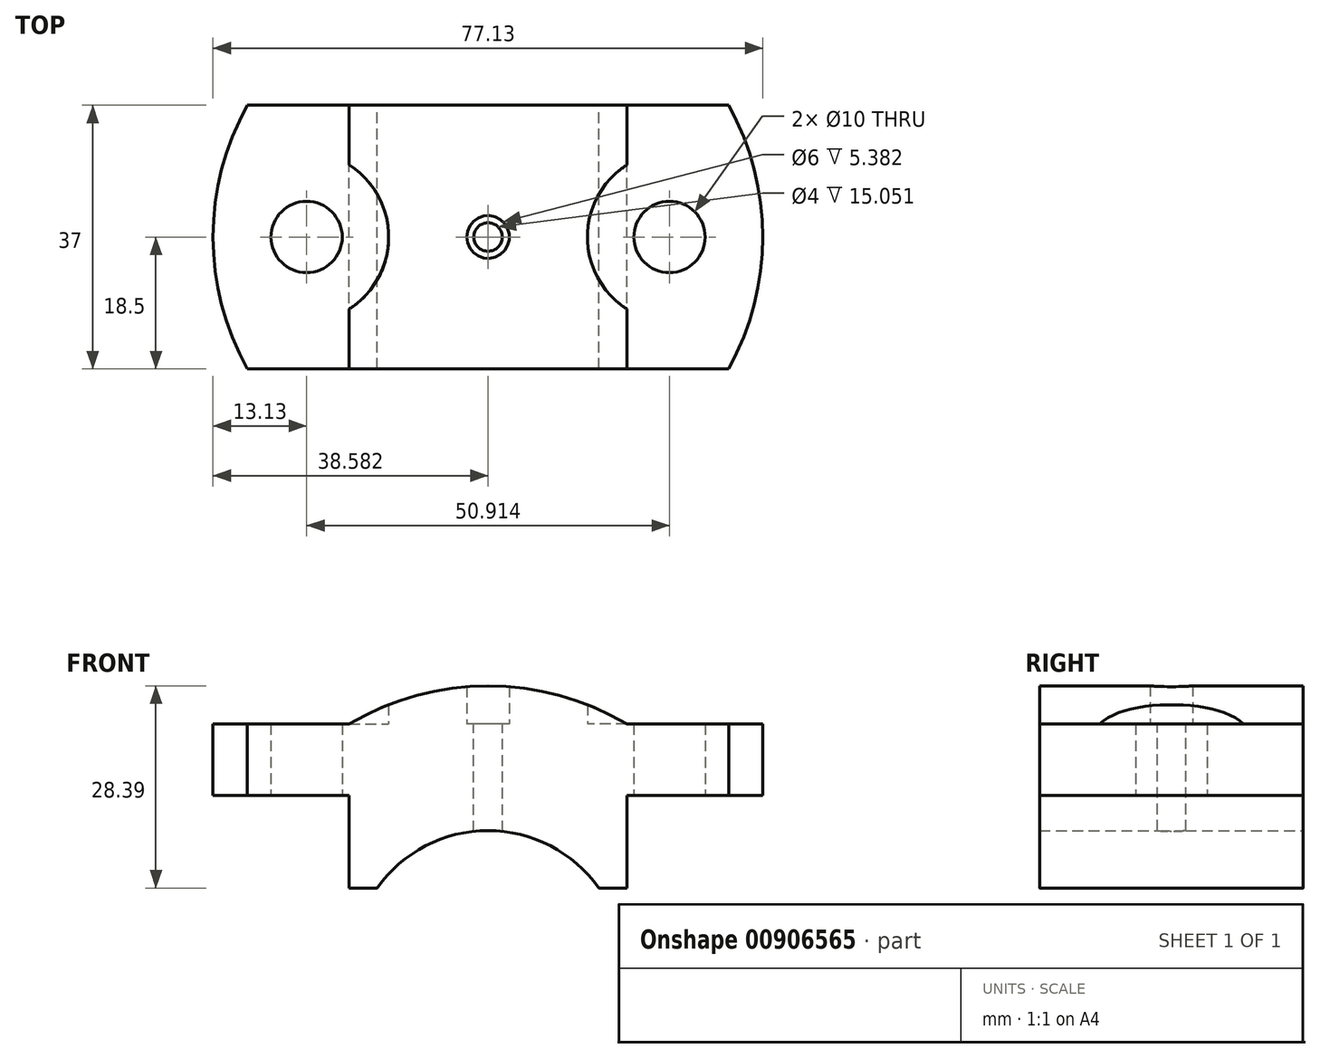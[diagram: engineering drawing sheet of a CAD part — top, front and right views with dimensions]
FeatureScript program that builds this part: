
annotation { "Feature Type Name" : "Feature", "Feature Type Description" : "" }
export const myFeature = defineFeature(function(context is Context, id is Id, definition is map)
    precondition{}
    {
        {
            var Q0;
            Q0=qCreatedBy(makeId("Front.planeOp"),FACE);
            var sketch = newSketch(context, id + "F0", { "sketchPlane" : qUnion([Q0])});
            skLineSegment(sketch, "E0", {"start": v(-114.53, 59.89) * mm, "end": v(-114.55, 46.89) * mm});
            skLineSegment(sketch, "E1", {"start": v(-75.54, 59.89) * mm, "end": v(-75.54, 46.89) * mm});
            skLineSegment(sketch, "E2", {"start": v(-114.55, 46.89) * mm, "end": v(-110.58, 46.88) * mm});
            skLineSegment(sketch, "E3", {"start": v(-75.54, 46.89) * mm, "end": v(-79.51, 46.89) * mm});
            skArc(sketch, "E4", {"start": v(-79.51, 46.89) * mm, "mid": v(-95.05, 54.94) * mm, "end": v(-110.58, 46.88) * mm});
            skLineSegment(sketch, "E5", {"start": v(-114.53, 59.89) * mm, "end": v(-75.54, 59.89) * mm});
            skSolve(sketch);
        }
        {
            var Q0;
            Q0 = qSketchRegion(id + "F0", true);
            extrude(context, id + "F1", {"entities" : qUnion([Q0]), "depth" : 37 * mm, "offsetDistance" : 25.4 * mm});
        }
        {
            var Q0;
            Q0=makeQuery(id+"F1.opExtrude","SWEPT_FACE",FACE,{"disambiguationData":[OSD([sQuery(id+"F0.wireOp",EDGE,"E5")])]});
            var sketch = newSketch(context, id + "F2", { "sketchPlane" : qUnion([Q0])});
            skCircle(sketch, "E6", {"center": v(-95.04, -18.5) * mm, "radius": 2 * mm});
            skPoint(sketch, "E6.centerSnap0", {"position": v(-114.53, -18.5) * mm});
            skPoint(sketch, "E6.centerSnap1", {"position": v(-95.04, -37) * mm});
            skSolve(sketch);
        }
        {
            var Q0;
            Q0=makeQuery(id+"F2.imprint","IMPRINT",FACE,{"disambiguationData":[TD([[makeQuery(id+"F2.imprint","IMPRINT",EDGE,{"derivedFrom":sQuery(id+"F2.wireOp",EDGE,"E6")}),1.0]])]});
            extrude(context, id + "F3", {"entities" : qUnion([Q0]), "operationType" : NewBodyOperationType.REMOVE, "oppositeDirection" : true, "depth" : 25.4 * mm, "offsetDistance" : 25.4 * mm});
        }
        {
            var Q0;
            Q0=makeQuery(id+"F1.opExtrude","SWEPT_FACE",FACE,{"disambiguationData":[OSD([sQuery(id+"F0.wireOp",EDGE,"E5")])]});
            var sketch = newSketch(context, id + "F4", { "sketchPlane" : qUnion([Q0])});
            skCircle(sketch, "E7", {"center": v(-95.04, -18.5) * mm, "radius": 2 * mm});
            skLineSegment(sketch, "E8", {"start": v(-61.28, -37) * mm, "end": v(-128.8, -37) * mm});
            skLineSegment(sketch, "E9", {"start": v(-128.8, 0) * mm, "end": v(-61.28, 0) * mm});
            skArc(sketch, "E10", {"start": v(-61.28, -37) * mm, "mid": v(-56.5, -18.5) * mm, "end": v(-61.28, 0) * mm});
            skArc(sketch, "E11", {"start": v(-128.8, 0) * mm, "mid": v(-133.62, -18.5) * mm, "end": v(-128.8, -37) * mm});
            skCircle(sketch, "E12", {"center": v(-69.58, -18.5) * mm, "radius": 5 * mm});
            skCircle(sketch, "E13", {"center": v(-120.49, -18.5) * mm, "radius": 5 * mm});
            skSolve(sketch);
        }
        {
            var Q0;
            {var subQ4=sQuery(id+"F4.wireOp",EDGE,"E10");Q0=makeQuery(id+"F4.imprint","IMPRINT",FACE,{"disambiguationData":[TD([[makeQuery(id+"F4.imprint","IMPRINT",EDGE,{"derivedFrom":subQ4}),1.0]])]});}
            var Q1;
            Q1=makeQuery(id+"F2.imprint","IMPRINT",FACE,{"disambiguationData":[TD([[makeQuery(id+"F2.imprint","IMPRINT",EDGE,{"derivedFrom":sQuery(id+"F2.wireOp",EDGE,"E6")}),-1.0]])]});
            var Q2;
            {var subQ2=sQuery(id+"F4.wireOp",EDGE,"E11");Q2=makeQuery(id+"F4.imprint","IMPRINT",FACE,{"disambiguationData":[TD([[makeQuery(id+"F4.imprint","IMPRINT",EDGE,{"derivedFrom":subQ2}),1.0]])]});}
            extrude(context, id + "F5", {"entities" : qUnion([Q0, Q1, Q2]), "operationType" : NewBodyOperationType.ADD, "depth" : 10 * mm, "offsetDistance" : 25.4 * mm});
        }
        {
            var Q0;
            {var subQ0=sQuery(id+"F4.wireOp",EDGE,"E9");var subQ1=sQuery(id+"F4.wireOp",EDGE,"E8");var subQ2=sQuery(id+"F0.wireOp",EDGE,"E5");var subQ3=sQuery(id+"F0.wireOp",EDGE,"E0");var subQ4=sQuery(id+"F0.wireOp",EDGE,"E1");Q0=makeQuery(id+"F5.boolean.opBoolean","MERGE",FACE,{"derivedFrom":[makeQuery(id+"F5.opExtrude","CAP_FACE",FACE,{"disambiguationData":[OSD([subQ3,subQ4,subQ2,sQuery(id+"F2.wireOp",EDGE,"E6")])],"isStart":false}),makeQuery(id+"F5.opExtrude","CAP_FACE",FACE,{"disambiguationData":[OSD([subQ4,subQ2,subQ1,subQ0,sQuery(id+"F4.wireOp",EDGE,"E10"),sQuery(id+"F4.wireOp",EDGE,"E12")])],"isStart":false}),makeQuery(id+"F5.opExtrude","CAP_FACE",FACE,{"disambiguationData":[OSD([subQ3,subQ2,subQ1,subQ0,sQuery(id+"F4.wireOp",EDGE,"E11"),sQuery(id+"F4.wireOp",EDGE,"E13")])],"isStart":false})]});}
            var sketch = newSketch(context, id + "F6", { "sketchPlane" : qUnion([Q0])});
            skLineSegment(sketch, "E14", {"start": v(-114.53, 0) * mm, "end": v(-114.53, -8.38) * mm});
            skLineSegment(sketch, "E15", {"start": v(-114.53, -37) * mm, "end": v(-114.53, -28.62) * mm});
            skLineSegment(sketch, "E16", {"start": v(-75.54, 0) * mm, "end": v(-75.54, -8.38) * mm});
            skLineSegment(sketch, "E17", {"start": v(-75.54, -37) * mm, "end": v(-75.54, -28.62) * mm});
            skArc(sketch, "E18", {"start": v(-114.53, -28.62) * mm, "mid": v(-108.98, -18.5) * mm, "end": v(-114.53, -8.38) * mm});
            skArc(sketch, "E19", {"start": v(-75.54, -8.38) * mm, "mid": v(-81.1, -18.5) * mm, "end": v(-75.54, -28.62) * mm});
            skCircle(sketch, "E20", {"center": v(-95.04, -18.5) * mm, "radius": 3 * mm});
            skSolve(sketch);
        }
        {
            var Q0;
            Q0=makeQuery(id+"F6.imprint","IMPRINT",FACE,{"disambiguationData":[TD([[makeQuery(id+"F6.imprint","IMPRINT",EDGE,{"derivedFrom":sQuery(id+"F6.wireOp",EDGE,"E14")}),1.0]])]});
            extrude(context, id + "F7", {"entities" : qUnion([Q0]), "operationType" : NewBodyOperationType.ADD, "depth" : 10 * mm, "offsetDistance" : 25.4 * mm});
        }
        {
            var Q0;
            {var subQ0=sQuery(id+"F4.wireOp",EDGE,"E9");var subQ1=sQuery(id+"F0.wireOp",EDGE,"E5");var subQ2=sQuery(id+"F0.wireOp",EDGE,"E1");var subQ3=sQuery(id+"F0.wireOp",EDGE,"E0");Q0=makeQuery(id+"F7.boolean.opBoolean","MERGE",FACE,{"derivedFrom":[makeQuery(id+"F5.boolean.opBoolean","MERGE",FACE,{"derivedFrom":[makeQuery(id+"F1.opExtrude","CAP_FACE",FACE,{"disambiguationData":[OSD([subQ3,subQ2,sQuery(id+"F0.wireOp",EDGE,"E2"),sQuery(id+"F0.wireOp",EDGE,"E3"),sQuery(id+"F0.wireOp",EDGE,"E4"),subQ1])],"isStart":true}),makeQuery(id+"F5.opExtrude","SWEPT_FACE",FACE,{"disambiguationData":[OSD([subQ1]),TDD([makeQuery(id+"F2.imprint","IMPRINT",EDGE,{"derivedFrom":makeQuery(id+"F1.opExtrude","CAP_EDGE",EDGE,{"disambiguationData":[OSD([subQ1])],"isStart":true})})])]}),makeQuery(id+"F5.opExtrude","SWEPT_FACE",FACE,{"disambiguationData":[OSD([subQ0]),TDD([makeQuery(id+"F4.imprint","IMPRINT",EDGE,{"disambiguationData":[TD([[makeQuery(id+"F4.imprint","INTERSECT",VERTEX,{"derivedFrom":[subQ0,sQuery(id+"F4.wireOp",EDGE,"E11")]}),-1.0]])],"derivedFrom":subQ0})])]}),makeQuery(id+"F5.opExtrude","SWEPT_FACE",FACE,{"disambiguationData":[OSD([subQ0]),TDD([makeQuery(id+"F4.imprint","IMPRINT",EDGE,{"disambiguationData":[TD([[makeQuery(id+"F4.imprint","INTERSECT",VERTEX,{"derivedFrom":[subQ0,sQuery(id+"F4.wireOp",EDGE,"E10")]}),1.0]])],"derivedFrom":subQ0})])]})]}),makeQuery(id+"F7.opExtrude","SWEPT_FACE",FACE,{"disambiguationData":[OSD([subQ1,subQ0])]})]});}
            var sketch = newSketch(context, id + "F8", { "sketchPlane" : qUnion([Q0])});
            skArc(sketch, "E21", {"start": v(114.53, 69.89) * mm, "mid": v(95.04, 75.27) * mm, "end": v(75.54, 69.89) * mm});
            skSolve(sketch);
        }
        {
            var Q0;
            {var subQ2=sQuery(id+"F4.wireOp",EDGE,"E9");var subQ4=sQuery(id+"F0.wireOp",EDGE,"E5");var subQ6=sQuery(id+"F6.wireOp",EDGE,"E16");var subQ12=makeQuery(id+"F7.opExtrude","SWEPT_EDGE",EDGE,{"disambiguationData":[OSD([subQ4,subQ2,subQ6])]});Q0=makeQuery(id+"F8.imprint","IMPRINT",FACE,{"disambiguationData":[TD([[makeQuery(id+"F8.imprint","IMPRINT",EDGE,{"derivedFrom":subQ12}),1.0]])]});}
            var Q1;
            {var subQ2=sQuery(id+"F4.wireOp",EDGE,"E9");var subQ4=sQuery(id+"F0.wireOp",EDGE,"E5");var subQ8=sQuery(id+"F6.wireOp",EDGE,"E14");var subQ12=makeQuery(id+"F7.opExtrude","SWEPT_EDGE",EDGE,{"disambiguationData":[OSD([subQ4,subQ2,subQ8])]});Q1=makeQuery(id+"F8.imprint","IMPRINT",FACE,{"disambiguationData":[TD([[makeQuery(id+"F8.imprint","IMPRINT",EDGE,{"derivedFrom":subQ12}),-1.0]])]});}
            extrude(context, id + "F9", {"entities" : qUnion([Q0, Q1]), "operationType" : NewBodyOperationType.REMOVE, "oppositeDirection" : true, "depth" : 25.4 * mm, "offsetDistance" : 25.4 * mm});
        }
        {
            var Q0;
            {var subQ0=sQuery(id+"F4.wireOp",EDGE,"E8");var subQ1=sQuery(id+"F0.wireOp",EDGE,"E5");var subQ2=sQuery(id+"F0.wireOp",EDGE,"E0");var subQ3=sQuery(id+"F0.wireOp",EDGE,"E1");Q0=makeQuery(id+"F7.boolean.opBoolean","MERGE",FACE,{"derivedFrom":[makeQuery(id+"F5.boolean.opBoolean","MERGE",FACE,{"derivedFrom":[makeQuery(id+"F1.opExtrude","CAP_FACE",FACE,{"disambiguationData":[OSD([subQ2,subQ3,sQuery(id+"F0.wireOp",EDGE,"E2"),sQuery(id+"F0.wireOp",EDGE,"E3"),sQuery(id+"F0.wireOp",EDGE,"E4"),subQ1])],"isStart":false}),makeQuery(id+"F5.opExtrude","SWEPT_FACE",FACE,{"disambiguationData":[OSD([subQ1]),TDD([makeQuery(id+"F2.imprint","IMPRINT",EDGE,{"derivedFrom":makeQuery(id+"F1.opExtrude","CAP_EDGE",EDGE,{"disambiguationData":[OSD([subQ1])],"isStart":false})})])]}),makeQuery(id+"F5.opExtrude","SWEPT_FACE",FACE,{"disambiguationData":[OSD([subQ0]),TDD([makeQuery(id+"F4.imprint","IMPRINT",EDGE,{"disambiguationData":[TD([[makeQuery(id+"F4.imprint","INTERSECT",VERTEX,{"derivedFrom":[makeQuery(id+"F1.opExtrude","SWEPT_EDGE",EDGE,{"disambiguationData":[OSD([subQ3,subQ1])]}),subQ0]}),1.0],[makeQuery(id+"F4.imprint","INTERSECT",VERTEX,{"derivedFrom":[subQ0,sQuery(id+"F4.wireOp",EDGE,"E10")]}),-1.0]])],"derivedFrom":subQ0})])]}),makeQuery(id+"F5.opExtrude","SWEPT_FACE",FACE,{"disambiguationData":[OSD([subQ0]),TDD([makeQuery(id+"F4.imprint","IMPRINT",EDGE,{"disambiguationData":[TD([[makeQuery(id+"F4.imprint","INTERSECT",VERTEX,{"derivedFrom":[makeQuery(id+"F1.opExtrude","SWEPT_EDGE",EDGE,{"disambiguationData":[OSD([subQ2,subQ1])]}),subQ0]}),-1.0],[makeQuery(id+"F4.imprint","INTERSECT",VERTEX,{"derivedFrom":[subQ0,sQuery(id+"F4.wireOp",EDGE,"E11")]}),1.0]])],"derivedFrom":subQ0})])]})]}),makeQuery(id+"F7.opExtrude","SWEPT_FACE",FACE,{"disambiguationData":[OSD([subQ1,subQ0])]})]});}
            var sketch = newSketch(context, id + "F10", { "sketchPlane" : qUnion([Q0])});
            skArc(sketch, "E22", {"start": v(-75.54, 69.89) * mm, "mid": v(-95.04, 75.27) * mm, "end": v(-114.53, 69.89) * mm});
            skSolve(sketch);
        }
        {
            var Q0;
            Q0=makeQuery(id+"F10.imprint","IMPRINT",FACE,{"disambiguationData":[TD([[makeQuery(id+"F10.imprint","IMPRINT",EDGE,{"derivedFrom":sQuery(id+"F10.wireOp",EDGE,"E22")}),-1.0]])]});
            extrude(context, id + "F11", {"entities" : qUnion([Q0]), "operationType" : NewBodyOperationType.REMOVE, "oppositeDirection" : true, "depth" : 25.4 * mm, "offsetDistance" : 25.4 * mm});
        }
    });
